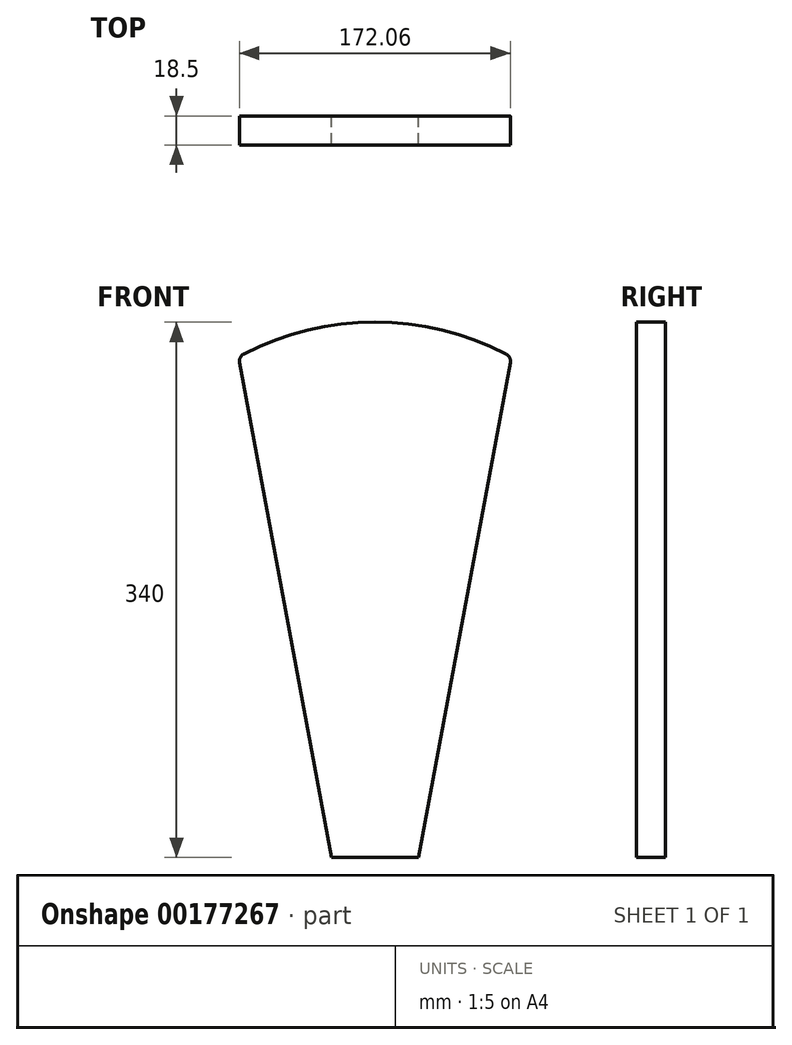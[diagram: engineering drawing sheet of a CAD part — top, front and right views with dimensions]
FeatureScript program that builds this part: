
annotation { "Feature Type Name" : "Feature", "Feature Type Description" : "" }
export const myFeature = defineFeature(function(context is Context, id is Id, definition is map)
    precondition{}
    {
        {
            var Q0;
            Q0=qCreatedBy(makeId("Front.planeOp"),FACE);
            var sketch = newSketch(context, id + "F0", { "sketchPlane" : qUnion([Q0])});
            skLineSegment(sketch, "E0", {"start": v(0, 340) * mm, "end": v(0, 0) * mm, "construction": true});
            skLineSegment(sketch, "E1", {"start": v(27.65, 0) * mm, "end": v(86.62, 318.17) * mm});
            skLineSegment(sketch, "E2.MirrorCS", {"start": v(-27.65, 0) * mm, "end": v(-86.62, 318.17) * mm});
            skLineSegment(sketch, "E3", {"start": v(-27.65, 0) * mm, "end": v(27.65, 0) * mm});
            skPoint(sketch, "E4", {"position": v(0, 0) * mm});
            skArc(sketch, "E5", {"start": v(86.62, 318.17) * mm, "mid": v(0, 340) * mm, "end": v(-86.62, 318.17) * mm});
            skSolve(sketch);
        }
        {
            var Q0;
            Q0 = qSketchRegion(id + "F0", true);
            extrude(context, id + "F1", {"entities" : qUnion([Q0]), "depth" : 18.5 * mm});
        }
        {
            var Q0;
            Q0=makeQuery(id+"F1.opExtrude","SWEPT_EDGE",EDGE,{"disambiguationData":[OSD([sQuery(id+"F0.wireOp",EDGE,"E2.MirrorCS"),sQuery(id+"F0.wireOp",EDGE,"E5")])]});
            fillet(context, id + "F2", {"entities" : qUnion([Q0]), "radius" : 5 * mm, "tangentPropagation" : true, "allowEdgeOverflow" : false});
        }
        {
            var Q0;
            Q0=makeQuery(id+"F1.opExtrude","SWEPT_EDGE",EDGE,{"disambiguationData":[OSD([sQuery(id+"F0.wireOp",EDGE,"E1"),sQuery(id+"F0.wireOp",EDGE,"E5")])]});
            fillet(context, id + "F3", {"entities" : qUnion([Q0]), "radius" : 5 * mm, "tangentPropagation" : true, "allowEdgeOverflow" : false});
        }
    });
